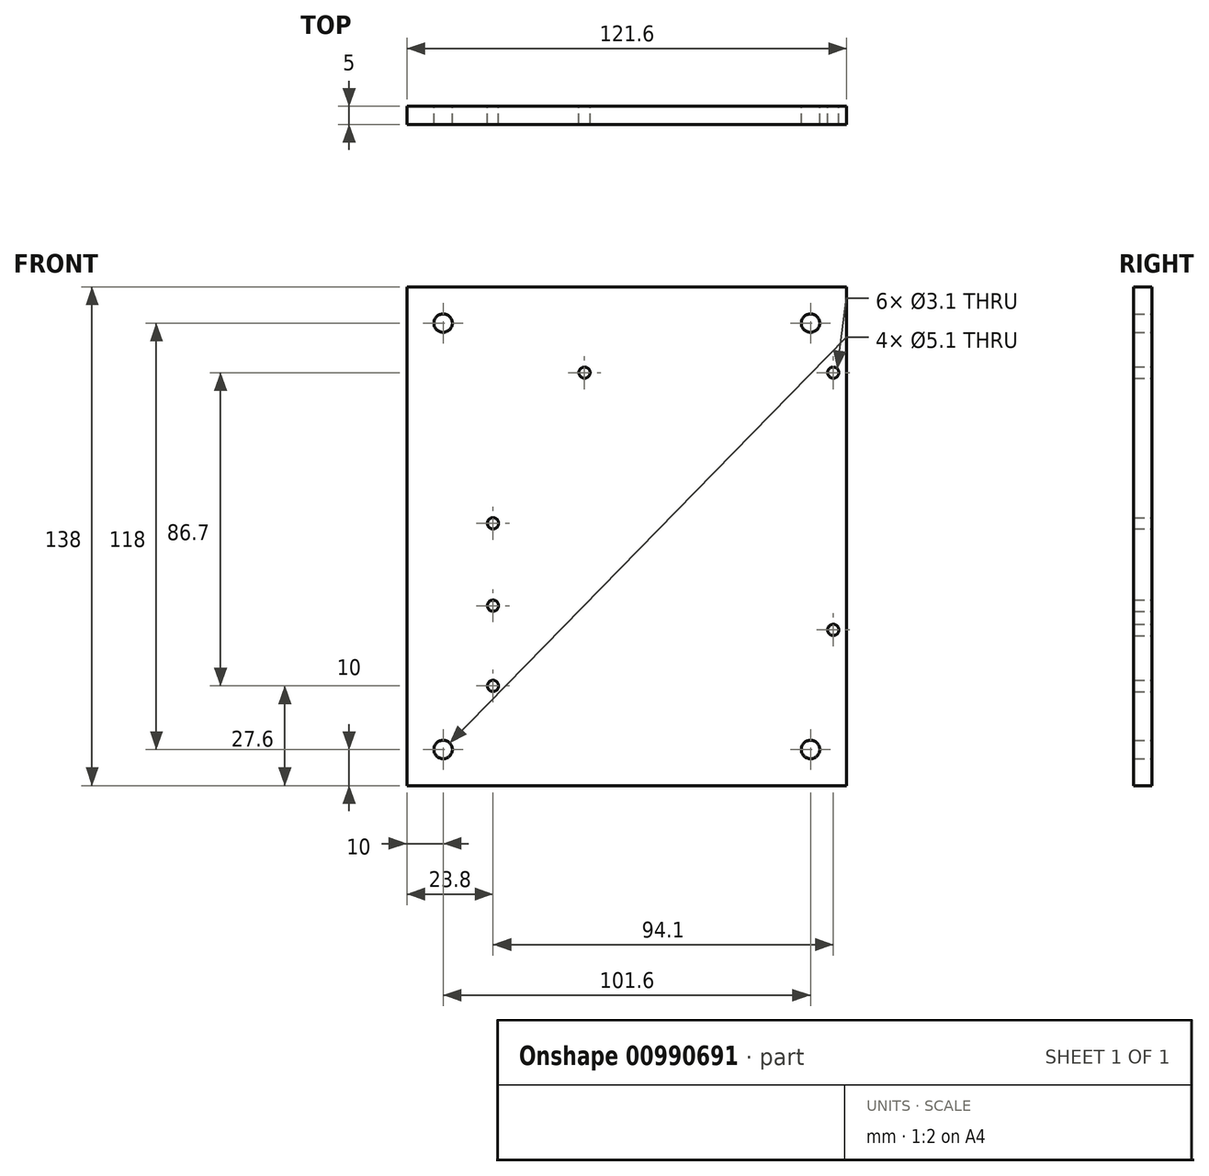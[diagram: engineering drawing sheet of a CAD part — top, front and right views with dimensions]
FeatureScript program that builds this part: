
annotation { "Feature Type Name" : "Feature", "Feature Type Description" : "" }
export const myFeature = defineFeature(function(context is Context, id is Id, definition is map)
    precondition{}
    {
        {
            var Q0;
            Q0=qCreatedBy(makeId("Front.planeOp"),FACE);
            var sketch = newSketch(context, id + "F0", { "sketchPlane" : qUnion([Q0])});
            skLineSegment(sketch, "E0.bottom", {"start": v(60.8, -69) * mm, "end": v(-60.8, -69) * mm});
            skLineSegment(sketch, "E0.top", {"start": v(60.8, 69) * mm, "end": v(-60.8, 69) * mm});
            skLineSegment(sketch, "E0.left", {"start": v(60.8, -69) * mm, "end": v(60.8, 69) * mm});
            skLineSegment(sketch, "E0.right", {"start": v(-60.8, -69) * mm, "end": v(-60.8, 69) * mm});
            skPoint(sketch, "E0.middle", {"position": v(0, 0) * mm});
            skCircle(sketch, "E1", {"center": v(50.8, 59) * mm, "radius": 2.55 * mm});
            skCircle(sketch, "E2.MirrorC", {"center": v(-50.8, 59) * mm, "radius": 2.55 * mm});
            skCircle(sketch, "E3.MirrorC", {"center": v(-50.8, -59) * mm, "radius": 2.55 * mm});
            skCircle(sketch, "E4.MirrorC", {"center": v(50.8, -59) * mm, "radius": 2.55 * mm});
            skLineSegment(sketch, "E5.bottom", {"start": v(60.8, -49) * mm, "end": v(-60.8, -49) * mm, "construction": true});
            skLineSegment(sketch, "E5.top", {"start": v(60.8, 49) * mm, "end": v(-60.8, 49) * mm, "construction": true});
            skLineSegment(sketch, "E5.left", {"start": v(60.8, -49) * mm, "end": v(60.8, 49) * mm, "construction": true});
            skLineSegment(sketch, "E5.right", {"start": v(-60.8, -49) * mm, "end": v(-60.8, 49) * mm, "construction": true});
            skCircle(sketch, "E6", {"center": v(57.1, 45.3) * mm, "radius": 1.55 * mm});
            skCircle(sketch, "E7", {"center": v(57.1, -25.9) * mm, "radius": 1.55 * mm});
            skCircle(sketch, "E8", {"center": v(-11.7, 45.3) * mm, "radius": 1.55 * mm});
            skLineSegment(sketch, "E9", {"start": v(-37, -49) * mm, "end": v(-37, 3.6) * mm, "construction": true});
            skCircle(sketch, "E10", {"center": v(-37, 3.6) * mm, "radius": 1.55 * mm});
            skCircle(sketch, "E11", {"center": v(-37, -19.2) * mm, "radius": 1.55 * mm});
            skCircle(sketch, "E12", {"center": v(-37, -41.4) * mm, "radius": 1.55 * mm});
            skSolve(sketch);
        }
        {
            var Q0;
            Q0 = qSketchRegion(id + "F0", true);
            extrude(context, id + "F1", {"entities" : qUnion([Q0]), "depth" : 5 * mm, "offsetDistance" : 25 * mm});
        }
    });
